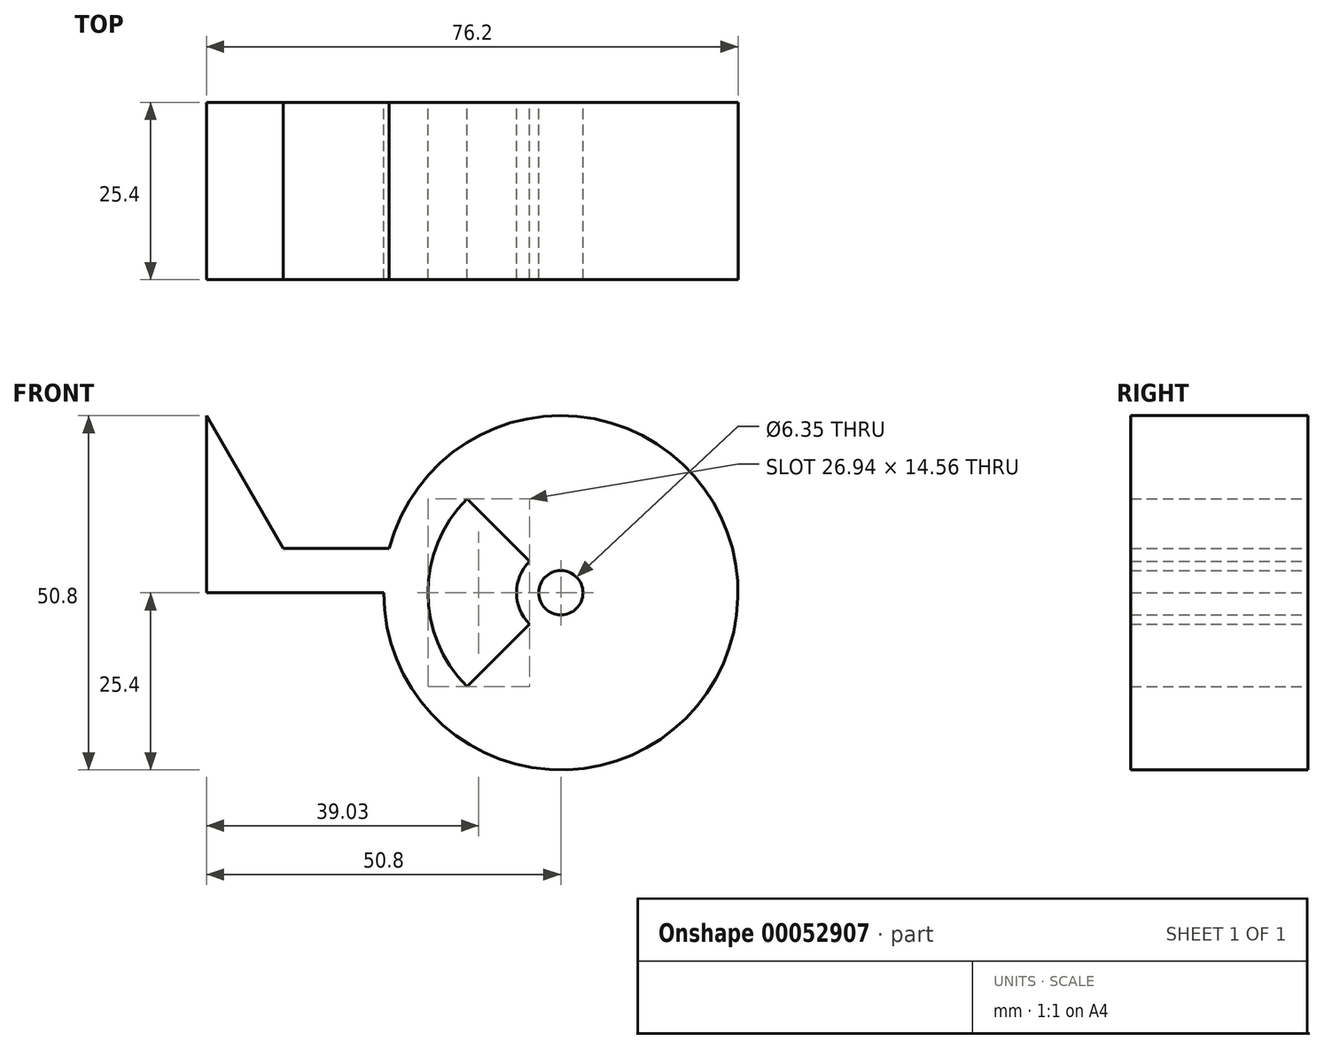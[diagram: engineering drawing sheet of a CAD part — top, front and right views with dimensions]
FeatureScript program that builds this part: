
annotation { "Feature Type Name" : "Feature", "Feature Type Description" : "" }
export const myFeature = defineFeature(function(context is Context, id is Id, definition is map)
    precondition{}
    {
        {
            var Q0;
            Q0=qCreatedBy(makeId("Front.planeOp"),FACE);
            var sketch = newSketch(context, id + "F0", { "sketchPlane" : qUnion([Q0])});
            skArc(sketch, "E0", {"start": v(-25.4, 0) * mm, "mid": v(25.2, -3.2) * mm, "end": v(-24.6, 6.35) * mm});
            skCircle(sketch, "E1", {"center": v(0, 0) * mm, "radius": 3.18 * mm});
            skLineSegment(sketch, "E2", {"start": v(-50.8, 0) * mm, "end": v(-50.8, 25.4) * mm});
            skLineSegment(sketch, "E3", {"start": v(-50.8, 25.4) * mm, "end": v(-39.8, 6.35) * mm});
            skLineSegment(sketch, "E4.trimOffspring", {"start": v(-24.6, 6.35) * mm, "end": v(-39.8, 6.35) * mm});
            skLineSegment(sketch, "E5.trimOffspring", {"start": v(-25.4, 0) * mm, "end": v(-50.8, 0) * mm});
            skArc(sketch, "E6", {"start": v(-13.47, 13.47) * mm, "mid": v(-19.05, 0) * mm, "end": v(-13.47, -13.47) * mm});
            skPoint(sketch, "E7.center.orphan", {"position": v(-12.7, 0) * mm});
            skLineSegment(sketch, "E8", {"start": v(-4.5, 4.5) * mm, "end": v(-13.47, 13.47) * mm});
            skLineSegment(sketch, "E9", {"start": v(-4.5, -4.5) * mm, "end": v(-13.47, -13.47) * mm});
            skArc(sketch, "E10", {"start": v(-4.5, 4.5) * mm, "mid": v(-6.35, 0) * mm, "end": v(-4.5, -4.5) * mm});
            skSolve(sketch);
        }
        {
            var Q0;
            Q0=makeQuery(id+"F0.imprint","IMPRINT",FACE,{"disambiguationData":[TD([[makeQuery(id+"F0.imprint","IMPRINT",EDGE,{"derivedFrom":sQuery(id+"F0.wireOp",EDGE,"E0")}),1.0]])]});
            extrude(context, id + "F1", {"entities" : qUnion([Q0]), "depth" : 25.4 * mm});
        }
    });
